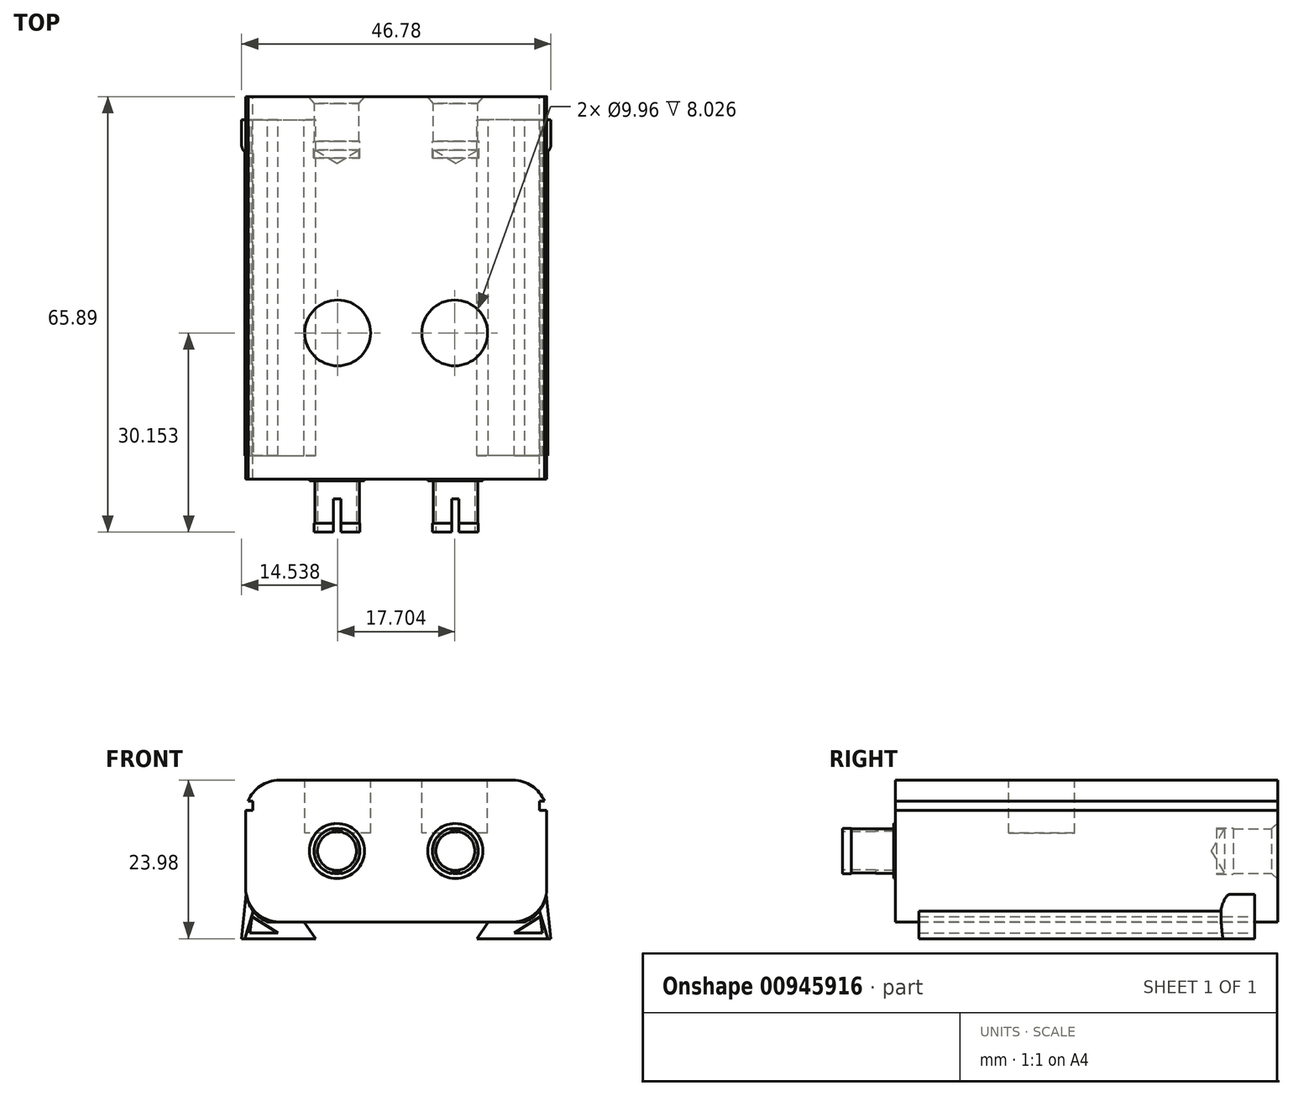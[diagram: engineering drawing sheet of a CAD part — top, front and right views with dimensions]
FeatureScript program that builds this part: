
annotation { "Feature Type Name" : "Feature", "Feature Type Description" : "" }
export const myFeature = defineFeature(function(context is Context, id is Id, definition is map)
    precondition{}
    {
        {
            var Q0;
            Q0=qCreatedBy(makeId("Top.planeOp"),FACE);
            var sketch = newSketch(context, id + "F0", { "sketchPlane" : qUnion([Q0])});
            skLineSegment(sketch, "E0.bottom", {"start": v(22.77, 28.93) * mm, "end": v(-22.77, 28.93) * mm});
            skLineSegment(sketch, "E0.top", {"start": v(22.77, -28.93) * mm, "end": v(-22.77, -28.93) * mm});
            skLineSegment(sketch, "E0.left", {"start": v(22.77, 28.93) * mm, "end": v(22.77, -28.93) * mm});
            skLineSegment(sketch, "E0.right", {"start": v(-22.77, 28.93) * mm, "end": v(-22.77, -28.93) * mm});
            skPoint(sketch, "E0.middle", {"position": v(0, 0) * mm});
            skSolve(sketch);
        }
        {
            var Q0;
            Q0 = qSketchRegion(id + "F0", true);
            extrude(context, id + "F1", {"entities" : qUnion([Q0]), "depth" : 21.44 * mm, "offsetDistance" : 25.4 * mm});
        }
        {
            var Q0;
            Q0=makeQuery(id+"F1.opExtrude","CAP_EDGE",EDGE,{"disambiguationData":[OSD([sQuery(id+"F0.wireOp",EDGE,"E0.right")])],"isStart":false});
            var Q1;
            Q1=makeQuery(id+"F1.opExtrude","CAP_EDGE",EDGE,{"disambiguationData":[OSD([sQuery(id+"F0.wireOp",EDGE,"E0.left")])],"isStart":false});
            var Q2;
            Q2=makeQuery(id+"F1.opExtrude","CAP_EDGE",EDGE,{"disambiguationData":[OSD([sQuery(id+"F0.wireOp",EDGE,"E0.left")])],"isStart":true});
            var Q3;
            Q3=makeQuery(id+"F1.opExtrude","CAP_EDGE",EDGE,{"disambiguationData":[OSD([sQuery(id+"F0.wireOp",EDGE,"E0.right")])],"isStart":true});
            fillet(context, id + "F2", {"entities" : qUnion([Q0, Q1, Q2, Q3]), "radius" : 5.08 * mm, "tangentPropagation" : true, "allowEdgeOverflow" : false});
        }
        {
            var Q0;
            Q0=makeQuery(id+"F1.opExtrude","SWEPT_FACE",FACE,{"disambiguationData":[OSD([sQuery(id+"F0.wireOp",EDGE,"E0.top")])]});
            var sketch = newSketch(context, id + "F3", { "sketchPlane" : qUnion([Q0])});
            skCircle(sketch, "E1", {"center": v(-8.95, 10.72) * mm, "radius": 4.17 * mm});
            skCircle(sketch, "E2.MirrorC", {"center": v(8.95, 10.72) * mm, "radius": 4.17 * mm});
            skSolve(sketch);
        }
        {
            var Q0;
            Q0 = qSketchRegion(id + "F3", true);
            extrude(context, id + "F4", {"entities" : qUnion([Q0]), "operationType" : NewBodyOperationType.ADD, "depth" : 0.25 * mm, "offsetDistance" : 25.4 * mm});
        }
        {
            var Q0;
            Q0=makeQuery(id+"F4.opExtrude","CAP_FACE",FACE,{"disambiguationData":[OSD([sQuery(id+"F3.wireOp",EDGE,"E1")])],"isStart":false});
            var sketch = newSketch(context, id + "F5", { "sketchPlane" : qUnion([Q0])});
            skCircle(sketch, "E3", {"center": v(-8.95, 10.72) * mm, "radius": 3.37 * mm});
            skCircle(sketch, "E4.MirrorC", {"center": v(8.95, 10.72) * mm, "radius": 3.37 * mm});
            skSolve(sketch);
        }
        {
            var Q0;
            Q0 = qSketchRegion(id + "F5", true);
            extrude(context, id + "F6", {"entities" : qUnion([Q0]), "operationType" : NewBodyOperationType.ADD, "depth" : 6.43 * mm, "offsetDistance" : 25.4 * mm});
        }
        {
            var Q0;
            Q0=makeQuery(id+"F6.opExtrude","CAP_FACE",FACE,{"disambiguationData":[OSD([sQuery(id+"F5.wireOp",EDGE,"E3")])],"isStart":false});
            var sketch = newSketch(context, id + "F7", { "sketchPlane" : qUnion([Q0])});
            skCircle(sketch, "E5", {"center": v(-8.95, 10.72) * mm, "radius": 3.47 * mm});
            skCircle(sketch, "E6.MirrorC", {"center": v(8.95, 10.72) * mm, "radius": 3.47 * mm});
            skSolve(sketch);
        }
        {
            var Q0;
            Q0 = qSketchRegion(id + "F7", true);
            extrude(context, id + "F8", {"entities" : qUnion([Q0]), "operationType" : NewBodyOperationType.ADD, "depth" : 1.35 * mm, "offsetDistance" : 25.4 * mm});
        }
        {
            var Q0;
            Q0=qCreatedBy(makeId("Top.planeOp"),FACE);
            var sketch = newSketch(context, id + "F9", { "sketchPlane" : qUnion([Q0])});
            skLineSegment(sketch, "E7.bottom", {"start": v(-9.47, -39.35) * mm, "end": v(-8.38, -39.35) * mm});
            skLineSegment(sketch, "E7.top", {"start": v(-9.47, -31.93) * mm, "end": v(-8.38, -31.93) * mm});
            skLineSegment(sketch, "E7.left", {"start": v(-9.47, -39.35) * mm, "end": v(-9.47, -31.93) * mm});
            skLineSegment(sketch, "E7.right", {"start": v(-8.38, -39.35) * mm, "end": v(-8.38, -31.93) * mm});
            skLineSegment(sketch, "E8.MirrorCS", {"start": v(9.47, -39.35) * mm, "end": v(9.47, -31.93) * mm});
            skLineSegment(sketch, "E9.MirrorCS", {"start": v(8.38, -39.35) * mm, "end": v(8.38, -31.93) * mm});
            skLineSegment(sketch, "E10.MirrorCS", {"start": v(9.47, -31.93) * mm, "end": v(8.38, -31.93) * mm});
            skLineSegment(sketch, "E11.MirrorCS", {"start": v(9.47, -39.35) * mm, "end": v(8.38, -39.35) * mm});
            skSolve(sketch);
        }
        {
            var Q0;
            Q0 = qSketchRegion(id + "F9", true);
            extrude(context, id + "F10", {"entities" : qUnion([Q0]), "operationType" : NewBodyOperationType.REMOVE, "endBound" : BoundingType.THROUGH_ALL, "depth" : 25.4 * mm, "offsetDistance" : 25.4 * mm});
        }
        {
            var Q0;
            {var subQ0=sQuery(id+"F7.wireOp",EDGE,"E5");Q0=makeQuery(id+"F10.boolean.opBoolean","SPLIT",FACE,{"disambiguationData":[TD([makeQuery(id+"F10.opExtrude","SWEPT_FACE",FACE,{"disambiguationData":[OSD([sQuery(id+"F9.wireOp",EDGE,"E7.right")])]})])],"derivedFrom":makeQuery(id+"F8.opExtrude","CAP_FACE",FACE,{"disambiguationData":[OSD([subQ0])],"isStart":false})});}
            var sketch = newSketch(context, id + "F11", { "sketchPlane" : qUnion([Q0])});
            skCircle(sketch, "E12", {"center": v(-8.95, 10.72) * mm, "radius": 2.94 * mm});
            skCircle(sketch, "E13.MirrorC", {"center": v(8.95, 10.72) * mm, "radius": 2.94 * mm});
            skSolve(sketch);
        }
        {
            var Q0;
            Q0 = qSketchRegion(id + "F11", true);
            var Q1;
            Q1=makeQuery(id+"F4.opExtrude","CAP_FACE",FACE,{"disambiguationData":[OSD([sQuery(id+"F3.wireOp",EDGE,"E1")])],"isStart":false});
            extrude(context, id + "F12", {"entities" : qUnion([Q0]), "operationType" : NewBodyOperationType.REMOVE, "endBound" : BoundingType.UP_TO_SURFACE, "oppositeDirection" : true, "depth" : 25.4 * mm, "endBoundEntityFace" : qUnion([Q1]), "offsetDistance" : 25.4 * mm});
        }
        {
            var Q0;
            Q0=makeQuery(id+"F1.opExtrude","SWEPT_FACE",FACE,{"disambiguationData":[OSD([sQuery(id+"F0.wireOp",EDGE,"E0.bottom")])]});
            var sketch = newSketch(context, id + "F13", { "sketchPlane" : qUnion([Q0])});
            skPoint(sketch, "E14", {"position": v(-9, 10.72) * mm});
            skPoint(sketch, "E15.MirrorP", {"position": v(9, 10.72) * mm});
            skSolve(sketch);
        }
        {
            var Q0;
            Q0=sQuery(id+"F13.wireOp",VERTEX,"E14");
            var Q1;
            Q1=sQuery(id+"F13.wireOp",VERTEX,"E15.MirrorP");
            var Q2;
            Q2=makeQuery(id+"F1.opExtrude","SWEPT_BODY",BODY,{"disambiguationData":[OSD([sQuery(id+"F0.wireOp",EDGE,"E0.bottom"),sQuery(id+"F0.wireOp",EDGE,"E0.top"),sQuery(id+"F0.wireOp",EDGE,"E0.left"),sQuery(id+"F0.wireOp",EDGE,"E0.right")])]});
            hole(context, id + "F14", {"style" : HoleStyle.C_SINK, "endStyle" : HoleEndStyle.BLIND, "holeDiameter" : 6.73 * mm, "cSinkDiameter" : 8.48 * mm, "cSinkAngle" : 82 * degree, "majorDiameter" : 6.35 * mm, "holeDepth" : 8.08 * mm, "isTappedThrough" : true, "tappedDepth" : 12.7 * mm, "tapClearance" : 3, "locations" : qUnion([Q0, Q1]), "scope" : qUnion([Q2])});
        }
        {
            var Q0;
            Q0=makeQuery(id+"F1.opExtrude","CAP_FACE",FACE,{"disambiguationData":[OSD([sQuery(id+"F0.wireOp",EDGE,"E0.bottom"),sQuery(id+"F0.wireOp",EDGE,"E0.top"),sQuery(id+"F0.wireOp",EDGE,"E0.left"),sQuery(id+"F0.wireOp",EDGE,"E0.right")])],"isStart":false});
            var sketch = newSketch(context, id + "F15", { "sketchPlane" : qUnion([Q0])});
            skCircle(sketch, "E16", {"center": v(-8.85, -6.8) * mm, "radius": 4.98 * mm});
            skCircle(sketch, "E17.MirrorC", {"center": v(8.85, -6.8) * mm, "radius": 4.98 * mm});
            skSolve(sketch);
        }
        {
            var Q0;
            Q0 = qSketchRegion(id + "F15", true);
            extrude(context, id + "F16", {"entities" : qUnion([Q0]), "operationType" : NewBodyOperationType.REMOVE, "oppositeDirection" : true, "depth" : 8.03 * mm, "offsetDistance" : 25.4 * mm});
        }
        {
            var Q0;
            Q0=qCreatedBy(makeId("Front.planeOp"),FACE);
            var sketch = newSketch(context, id + "F17", { "sketchPlane" : qUnion([Q0])});
            skLineSegment(sketch, "E18", {"start": v(22.69, 4.15) * mm, "end": v(23.39, -2.54) * mm});
            skLineSegment(sketch, "E19", {"start": v(23.39, -2.54) * mm, "end": v(12.2, -2.54) * mm});
            skLineSegment(sketch, "E20", {"start": v(12.2, -2.54) * mm, "end": v(13.96, 0) * mm});
            skArc(sketch, "E21", {"start": v(19.44, 0) * mm, "mid": v(21.65, 1.62) * mm, "end": v(22.69, 4.15) * mm});
            skLineSegment(sketch, "E22", {"start": v(19.44, 0) * mm, "end": v(13.96, 0) * mm});
            skLineSegment(sketch, "E23.MirrorCS", {"start": v(-23.39, -2.54) * mm, "end": v(-12.2, -2.54) * mm});
            skLineSegment(sketch, "E24.MirrorCS", {"start": v(-22.69, 4.15) * mm, "end": v(-23.39, -2.54) * mm});
            skArc(sketch, "E25.MirrorCS", {"start": v(-19.44, 0) * mm, "mid": v(-21.65, 1.62) * mm, "end": v(-22.69, 4.15) * mm});
            skLineSegment(sketch, "E26.MirrorCS", {"start": v(-19.44, 0) * mm, "end": v(-13.96, 0) * mm});
            skLineSegment(sketch, "E27.MirrorCS", {"start": v(-12.2, -2.54) * mm, "end": v(-13.96, 0) * mm});
            skSolve(sketch);
        }
        {
            var Q0;
            Q0=makeQuery(id+"F17.imprint","IMPRINT",FACE,{"disambiguationData":[TD([[makeQuery(id+"F17.imprint","IMPRINT",EDGE,{"derivedFrom":sQuery(id+"F17.wireOp",EDGE,"E23.MirrorCS")}),1.0]])]});
            var Q1;
            Q1=makeQuery(id+"F17.imprint","IMPRINT",FACE,{"disambiguationData":[TD([[makeQuery(id+"F17.imprint","IMPRINT",EDGE,{"derivedFrom":sQuery(id+"F17.wireOp",EDGE,"E18")}),-1.0]])]});
            extrude(context, id + "F18", {"entities" : qUnion([Q0, Q1]), "depth" : 25.4 * mm, "offsetDistance" : 25.4 * mm, "hasSecondDirection" : true, "secondDirectionOppositeDirection" : true, "secondDirectionDepth" : 25.4 * mm});
        }
        {
            var Q0;
            Q0=makeQuery(id+"F18.opExtrude","CAP_FACE",FACE,{"disambiguationData":[OSD([sQuery(id+"F17.wireOp",EDGE,"E18"),sQuery(id+"F17.wireOp",EDGE,"E19"),sQuery(id+"F17.wireOp",EDGE,"E20"),sQuery(id+"F17.wireOp",EDGE,"E21"),sQuery(id+"F17.wireOp",EDGE,"E22")])],"isStart":true});
            var sketch = newSketch(context, id + "F19", { "sketchPlane" : qUnion([Q0])});
            skLineSegment(sketch, "E28", {"start": v(-21.81, 0.8) * mm, "end": v(-22.14, -1.7) * mm});
            skPoint(sketch, "E28.startSnap0", {"position": v(-23.04, 0.8) * mm});
            skLineSegment(sketch, "E29", {"start": v(-22.14, -1.7) * mm, "end": v(-17.88, -1.7) * mm});
            skLineSegment(sketch, "E30", {"start": v(-17.88, -1.7) * mm, "end": v(-21.81, 0.8) * mm});
            skLineSegment(sketch, "E31.MirrorCS", {"start": v(22.14, -1.7) * mm, "end": v(17.88, -1.7) * mm});
            skLineSegment(sketch, "E32.MirrorCS", {"start": v(17.88, -1.7) * mm, "end": v(21.81, 0.8) * mm});
            skLineSegment(sketch, "E33.MirrorCS", {"start": v(21.81, 0.8) * mm, "end": v(22.14, -1.7) * mm});
            skSolve(sketch);
        }
        {
            var Q0;
            Q0 = qSketchRegion(id + "F19", true);
            extrude(context, id + "F20", {"entities" : qUnion([Q0]), "operationType" : NewBodyOperationType.REMOVE, "endBound" : BoundingType.THROUGH_ALL, "oppositeDirection" : true, "depth" : 25.4 * mm, "offsetDistance" : 25.4 * mm});
        }
        {
            var Q0;
            Q0=makeQuery(id+"F18.opExtrude","CAP_FACE",FACE,{"disambiguationData":[OSD([sQuery(id+"F17.wireOp",EDGE,"E23.MirrorCS"),sQuery(id+"F17.wireOp",EDGE,"E24.MirrorCS"),sQuery(id+"F17.wireOp",EDGE,"E25.MirrorCS"),sQuery(id+"F17.wireOp",EDGE,"E26.MirrorCS"),sQuery(id+"F17.wireOp",EDGE,"E27.MirrorCS")])],"isStart":false});
            var sketch = newSketch(context, id + "F21", { "sketchPlane" : qUnion([Q0])});
            skArc(sketch, "E34", {"start": v(-22.69, 4.15) * mm, "mid": v(-22.34, 2.82) * mm, "end": v(-21.65, 1.62) * mm});
            skLineSegment(sketch, "E35", {"start": v(-22.69, 4.15) * mm, "end": v(-24.18, -3.28) * mm});
            skLineSegment(sketch, "E36", {"start": v(-24.18, -3.28) * mm, "end": v(-23.09, -3.1) * mm});
            skLineSegment(sketch, "E37", {"start": v(-23.09, -3.1) * mm, "end": v(-21.65, 1.62) * mm});
            skLineSegment(sketch, "E38.MirrorCS", {"start": v(23.09, -3.1) * mm, "end": v(21.65, 1.62) * mm});
            skLineSegment(sketch, "E39.MirrorCS", {"start": v(22.69, 4.15) * mm, "end": v(24.18, -3.28) * mm});
            skLineSegment(sketch, "E40.MirrorCS", {"start": v(24.18, -3.28) * mm, "end": v(23.09, -3.1) * mm});
            skArc(sketch, "E41.MirrorCS", {"start": v(22.69, 4.15) * mm, "mid": v(22.34, 2.82) * mm, "end": v(21.65, 1.62) * mm});
            skSolve(sketch);
        }
        {
            var Q0;
            Q0 = qSketchRegion(id + "F21", true);
            extrude(context, id + "F22", {"entities" : qUnion([Q0]), "operationType" : NewBodyOperationType.REMOVE, "oppositeDirection" : true, "depth" : 45.72 * mm, "offsetDistance" : 25.4 * mm});
        }
        {
            var Q0;
            Q0=makeQuery(id+"F22.boolean.opBoolean","INTERSECT",EDGE,{"derivedFrom":[makeQuery(id+"F18.opExtrude","SWEPT_FACE",FACE,{"disambiguationData":[OSD([sQuery(id+"F17.wireOp",EDGE,"E24.MirrorCS")])]}),makeQuery(id+"F22.opExtrude","CAP_FACE",FACE,{"disambiguationData":[OSD([sQuery(id+"F21.wireOp",EDGE,"E34"),sQuery(id+"F21.wireOp",EDGE,"E35"),sQuery(id+"F21.wireOp",EDGE,"E36"),sQuery(id+"F21.wireOp",EDGE,"E37")])],"isStart":false})]});
            fillet(context, id + "F23", {"entities" : qUnion([Q0]), "radius" : 1.27 * mm, "tangentPropagation" : true, "allowEdgeOverflow" : false});
        }
        {
            var Q0;
            Q0=makeQuery(id+"F22.boolean.opBoolean","INTERSECT",EDGE,{"derivedFrom":[makeQuery(id+"F18.opExtrude","SWEPT_FACE",FACE,{"disambiguationData":[OSD([sQuery(id+"F17.wireOp",EDGE,"E18")])]}),makeQuery(id+"F22.opExtrude","CAP_FACE",FACE,{"disambiguationData":[OSD([sQuery(id+"F21.wireOp",EDGE,"E38.MirrorCS"),sQuery(id+"F21.wireOp",EDGE,"E39.MirrorCS"),sQuery(id+"F21.wireOp",EDGE,"E40.MirrorCS"),sQuery(id+"F21.wireOp",EDGE,"E41.MirrorCS")])],"isStart":false})]});
            fillet(context, id + "F24", {"entities" : qUnion([Q0]), "radius" : 1.27 * mm, "tangentPropagation" : true, "allowEdgeOverflow" : false});
        }
        {
            var Q0;
            Q0=makeQuery(id+"F1.opExtrude","SWEPT_FACE",FACE,{"disambiguationData":[OSD([sQuery(id+"F0.wireOp",EDGE,"E0.bottom")])]});
            cPlane(context, id + "F25", {"entities" : qUnion([Q0]), "cplaneType" : CPlaneType.OFFSET, "offset" : 8.03 * mm, "oppositeDirection" : true, "width" : 152.4 * mm, "height" : 152.4 * mm});
        }
        {
            var Q0;
            Q0=qCreatedBy(id+"F25.planeOp",FACE);
            var sketch = newSketch(context, id + "F26", { "sketchPlane" : qUnion([Q0])});
            skCircle(sketch, "E42.0", {"center": v(-9, 10.72) * mm, "radius": 3.37 * mm});
            skCircle(sketch, "E43.0", {"center": v(9, 10.72) * mm, "radius": 3.37 * mm});
            skCircle(sketch, "E44", {"center": v(-9, 10.72) * mm, "radius": 3.5 * mm});
            skCircle(sketch, "E45.MirrorC", {"center": v(9, 10.72) * mm, "radius": 3.5 * mm});
            skSolve(sketch);
        }
        {
            var Q0;
            Q0 = qSketchRegion(id + "F26", true);
            var Q1;
            Q1 = qSketchRegion(id + "F28", true);
            extrude(context, id + "F27", {"entities" : qUnion([Q0, Q1]), "operationType" : NewBodyOperationType.REMOVE, "oppositeDirection" : true, "depth" : 1.27 * mm, "offsetDistance" : 25.4 * mm, "hasSecondDirection" : true, "secondDirectionOppositeDirection" : false, "secondDirectionDepth" : 1.27 * mm});
        }
        {
            var Q0;
            Q0=makeQuery(id+"F1.opExtrude","SWEPT_FACE",FACE,{"disambiguationData":[OSD([sQuery(id+"F0.wireOp",EDGE,"E0.bottom")])]});
            var sketch = newSketch(context, id + "F28", { "sketchPlane" : qUnion([Q0])});
            skLineSegment(sketch, "E46.bottom", {"start": v(22.77, 18.24) * mm, "end": v(21.7, 18.24) * mm});
            skLineSegment(sketch, "E46.top", {"start": v(22.77, 16.9) * mm, "end": v(21.7, 16.9) * mm});
            skLineSegment(sketch, "E46.left", {"start": v(22.77, 18.24) * mm, "end": v(22.77, 16.9) * mm});
            skLineSegment(sketch, "E46.right", {"start": v(21.7, 18.24) * mm, "end": v(21.7, 16.9) * mm});
            skLineSegment(sketch, "E47.MirrorCS", {"start": v(-22.77, 16.9) * mm, "end": v(-21.7, 16.9) * mm});
            skLineSegment(sketch, "E48.MirrorCS", {"start": v(-21.7, 18.24) * mm, "end": v(-21.7, 16.9) * mm});
            skLineSegment(sketch, "E49.MirrorCS", {"start": v(-22.77, 18.24) * mm, "end": v(-21.7, 18.24) * mm});
            skLineSegment(sketch, "E50.MirrorCS", {"start": v(-22.77, 18.24) * mm, "end": v(-22.77, 16.9) * mm});
            skLineSegment(sketch, "E51", {"start": v(22.77, 14.64) * mm, "end": v(22.77, 21.15) * mm});
            skSolve(sketch);
        }
        {
            var Q0;
            {var subQ0=sQuery(id+"F28.wireOp",EDGE,"E48.MirrorCS");var subQ8=sQuery(id+"F28.wireOp",EDGE,"E46.right");var subQ15=sQuery(id+"F28.wireOp",EDGE,"E46.left");var subQ16=sQuery(id+"F28.wireOp",EDGE,"E50.MirrorCS");Q0=qUnion([makeQuery(id+"F28.imprint","IMPRINT",FACE,{"disambiguationData":[TD([[makeQuery(id+"F28.imprint","IMPRINT",EDGE,{"derivedFrom":subQ16}),1.0]])]}),makeQuery(id+"F28.imprint","IMPRINT",FACE,{"disambiguationData":[TD([[makeQuery(id+"F28.imprint","IMPRINT",EDGE,{"derivedFrom":subQ15}),-1.0]])]}),makeQuery(id+"F28.imprint","IMPRINT",FACE,{"disambiguationData":[TD([[makeQuery(id+"F28.imprint","IMPRINT",EDGE,{"derivedFrom":subQ8}),1.0]])]}),makeQuery(id+"F28.imprint","IMPRINT",FACE,{"disambiguationData":[TD([[makeQuery(id+"F28.imprint","IMPRINT",EDGE,{"derivedFrom":subQ0}),-1.0]])]})]);}
            extrude(context, id + "F29", {"entities" : qUnion([Q0]), "operationType" : NewBodyOperationType.REMOVE, "endBound" : BoundingType.THROUGH_ALL, "oppositeDirection" : true, "depth" : 25.4 * mm, "offsetDistance" : 25.4 * mm});
        }
    });
